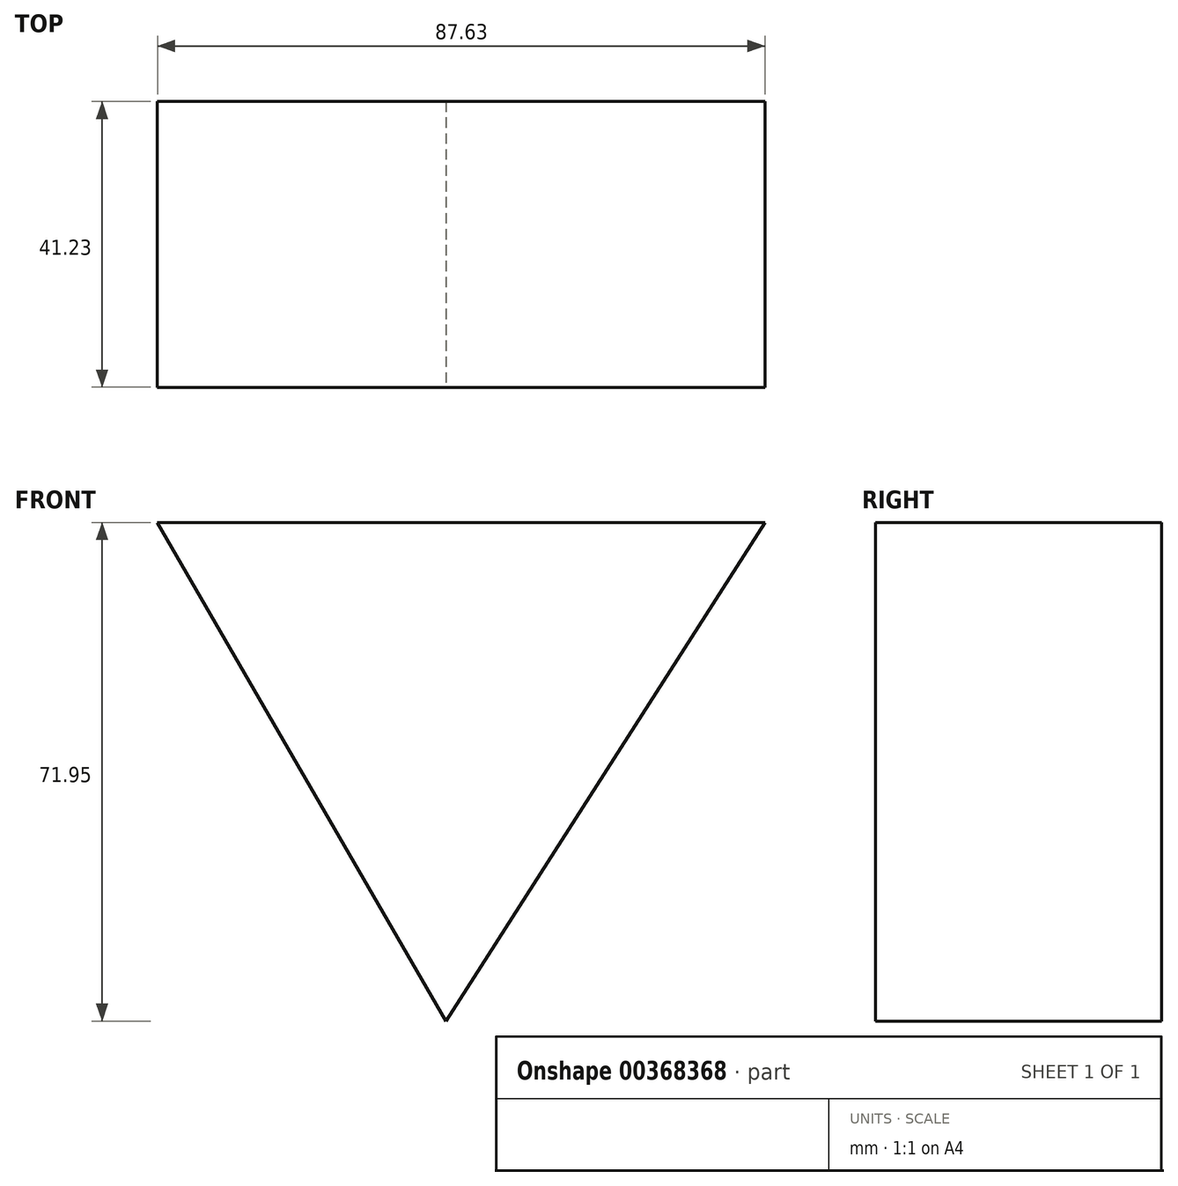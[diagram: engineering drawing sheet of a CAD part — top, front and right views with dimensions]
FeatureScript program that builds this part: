
annotation { "Feature Type Name" : "Feature", "Feature Type Description" : "" }
export const myFeature = defineFeature(function(context is Context, id is Id, definition is map)
    precondition{}
    {
        {
            var Q0;
            Q0=qCreatedBy(makeId("Front.planeOp"),FACE);
            var sketch = newSketch(context, id + "F0", { "sketchPlane" : qUnion([Q0])});
            skLineSegment(sketch, "E0", {"start": v(-41.64, 71.95) * mm, "end": v(0, 0) * mm});
            skLineSegment(sketch, "E1", {"start": v(0, 0) * mm, "end": v(45.99, 71.95) * mm});
            skLineSegment(sketch, "E2", {"start": v(45.99, 71.95) * mm, "end": v(-41.64, 71.95) * mm});
            skSolve(sketch);
        }
        {
            var Q0;
            Q0=sQuery(id+"F0.wireOp",EDGE,"E2");
            var Q1;
            Q1=sQuery(id+"F0.wireOp",EDGE,"E0");
            var Q2;
            Q2=sQuery(id+"F0.wireOp",EDGE,"E1");
            extrude(context, id + "F1", {"bodyType" : ToolBodyType.SURFACE, "surfaceEntities" : qUnion([Q0, Q1, Q2]), "depth" : 41.23 * mm});
        }
    });
